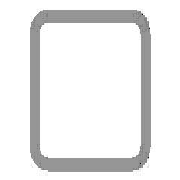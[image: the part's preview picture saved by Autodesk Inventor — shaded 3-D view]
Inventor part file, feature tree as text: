
AUTODESK INVENTOR PART (.ipt)
format: ipt  version: 2025.1 (Build 291241000, 241)  size: 211,456 bytes
history: native  units: mm (DEFAULTED — no unit token found)
features: other x14, sketch x4, extrude x3, plane x1
ambient origin geometry x8: Origin, YZ Plane, XZ Plane, XY Plane, X Axis, Y Axis, Z Axis, Center Point
bodies: Solid1 (feature_tree)
feature tree (22):
  parser-record x1  (decoder bookkeeping rows leaked as tree rows — omitted from the tree; the rows remain in map.json)
  other  "Driven Length"
  other  "Płaszczyzna początkowa"
  other  "Płaszczyzna końcowa"
  extrude  "Bryła"  TaperAngle=0.0deg  [1 undecoded]
  other  "Płaszczyzna konstrukcyjna4"
  other  "Płaszczyzna konstrukcyjna5"
  other  "Płaszczyzna konstrukcyjna6"
  extrude  "Wyciągnięcie proste2"  Depth=1700.0mm
  other  "Utwórz kombinację1"
  other  "Płaszczyzna konstrukcyjna7"
  other  "Płaszczyzna konstrukcyjna8"
  other  "Płaszczyzna konstrukcyjna9"
  extrude  "Wyciągnięcie proste3"  Depth=1700.0mm
  other  "Utwórz kombinację2"
  sketch  "Sketch3"  dims[d3=1700.0mm d4=0.0mm]
  plane  "Work Plane3"
  sketch  "Sketch4"  dims[d7=4.0mm d10=40.0mm d11=40.0mm d12=3.2mm d13=-0.0mm d14=1700.0mm d15=20.0mm d16=20.0mm d17=90.0deg d18=1700.0mm d19=0.13mm d20=0.0mm d21=0.13mm d22=0.0mm]
  sketch  "Szkic5"
  other  "Bryła2"
  sketch  "Szkic6"
  other  "Bryła3"
note: 1 required parameter value undecoded (feature->parameter linkage not recoverable at this tier; creation-order binding heuristic only, values carry confidence <= 0.55)
